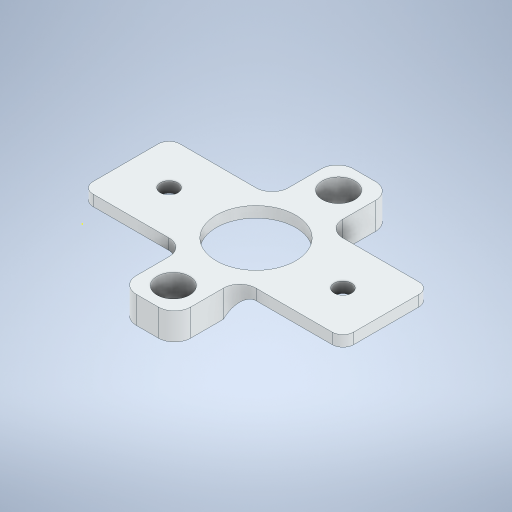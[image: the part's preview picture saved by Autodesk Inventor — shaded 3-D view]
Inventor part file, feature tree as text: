
AUTODESK INVENTOR PART (.ipt)
format: ipt  version: 2024 (Build 280153000, 153)  size: 620,032 bytes
history: native  units: in
note: dims shown in document units (in); Inventor stores cm internally (conversion verified against a paired STEP export)
features: sketch x20, extrude x18, projected_geometry x9, fillet x4
ambient origin geometry x8: Origin, YZ Plane, XZ Plane, XY Plane, X Axis, Y Axis, Z Axis, Center Point
bodies: Solid1 (feature_tree)
feature tree (51):
  sketch  "Sketch1"  dims[d0=47.6875in d1=0.0in d2=1.5in]
  extrude  "Extrusion1"  Depth=1.5in
  extrude  "Extrusion2"  Depth=0.344in
  extrude  "Extrusion3"  Depth=0.344in
  extrude  "Extrusion4"  Depth=0.17in
  extrude  "Extrusion5"  Depth=0.3594in TaperAngle=0.0deg
  extrude  "Extrusion6"  Depth=0.125in
  extrude  "Extrusion7"  Depth=1.0in TaperAngle=0.0deg
  extrude  "Extrusion8"  Depth=0.125in
  sketch  "Sketch13"  dims[d33=1.0in d34=2.7031in d35=0.0in d36=0.9844in d37=0.0in]
  extrude  "Extrusion9"  Depth=1.3594in TaperAngle=0.0deg
  extrude  "Extrusion10"  Depth=1.0in TaperAngle=0.0deg
  fillet  "Fillet1"  Radius=0.9844in
  extrude  "Extrusion11"  Depth=0.1875in
  extrude  "Extrusion12"  Depth=0.75in TaperAngle=0.0deg
  fillet  "Fillet3"  Radius=0.1875in
  extrude  "Extrusion13"  Depth=0.375in
  extrude  "Extrusion14"  Depth=0.1875in
  fillet  "Fillet4"  Radius=0.1875in
  extrude  "Extrusion15"  Depth=0.1875in
  extrude  "Extrusion17"  Depth=1.0in TaperAngle=0.0deg
  extrude  "Extrusion18"  Depth=0.375in TaperAngle=0.0deg
  extrude  "Extrusion19"  [1 undecoded]
  sketch  "Sketch2"  dims[d3=0.375in d4=0.344in]
  sketch  "Sketch3"  dims[d5=6.4375in d6=0.0in d7=0.344in]
  sketch  "Sketch5"  dims[d8=0.17in d9=0.17in]
  sketch  "Sketch7"  dims[d10=0.3594in d11=0.0in d12=0.3594in d13=0.0in]
  projected_geometry  "Projected Loop1"
  sketch  "Sketch8"  dims[d14=0.1249in d15=0.125in]
  sketch  "Sketch9"  dims[d16=1.0in d17=1.0781in d18=0.0in]
  sketch  "Sketch10"  dims[d19=1.103in d28=0.125in]
  projected_geometry  "Projected Loop2"
  sketch  "Sketch12"  dims[d29=1.0781in d30=0.0in d31=1.3594in d32=0.0in]
  sketch  "Sketch14"  dims[d38=0.1094in d39=0.0in d40=0.1875in]
  projected_geometry  "Projected Loop4"
  sketch  "Sketch15"  dims[d41=0.75in d42=0.0in d43=0.75in d44=0.0in d45=0.1875in]
  projected_geometry  "Projected Loop5"
  sketch  "Sketch16"  dims[d46=0.375in d47=0.375in]
  sketch  "Sketch17"  dims[d48=0.9511in d49=0.951in d50=0.1875in d51=0.0in]
  sketch  "Sketch18"  dims[d52=0.185in d53=0.0in d54=0.1875in]
  sketch  "Sketch19"  dims[d55=1.0in d56=0.0in d59=3.125in d60=0.0in]
  projected_geometry  "Projected Loop6"
  projected_geometry  "Projected Loop7"
  projected_geometry  "Projected Loop8"
  projected_geometry  "Projected Loop9"
  sketch  "Sketch20"  dims[d61=0.3125in d62=0.0in d63=0.375in d64=0.0in]
  projected_geometry  "Projected Loop10"
  sketch  "Sketch23"
  sketch  "Sketch24"
  sketch  "Sketch25"
  fillet  "Fillet2"  [1 undecoded]
note: 2 required parameter values undecoded (feature->parameter linkage not recoverable at this tier; creation-order binding heuristic only, values carry confidence <= 0.55)
